# Revit family: 210_c64ea0e677dc4fbe8cce54dced4735
name_source: partatom
category: Mechanical Equipment
revit_build: Autodesk Revit 2018 (Build: 20170223_1515(x64)
units: mm (PartAtom-declared; Revit-internal decimal feet)

## family parameters
Always vertical = Yes
Cut with Voids When Loaded = No
Part Type = Breaks Into
Room Calculation Point = No
Round Connector Dimension = Use Diameter
Shared = No
Work Plane-Based = No

## types (1)
- K2 REL W (700016)
    Clearance Zone Front Depth = 638 mm  [stored 2.09318 ft]
    DEXH = 125 mm
    DEXT = 125 mm
    DL = 48 mm  [stored 0.15748 ft]
    DOUT = 125 mm
    DSUP = 125 mm
    Description = K2 REL W (700016)
    EXHX = 215 mm  [stored 0.705381 ft]
    EXHY = 129 mm  [stored 0.423228 ft]
    EXTX = 72 mm  [stored 0.23622 ft]
    EXTY = 229 mm  [stored 0.751312 ft]
    H2 = 385 mm  [stored 1.26312 ft]
    L1 = 30 mm  [stored 0.0984252 ft]
    L1__ve = -30 mm
    L2 = 299 mm  [stored 0.980971 ft]
    LM = 538 mm
    MC Product Code = K2 REL W (700016)
    Manufacturer = Flexit
    OUTX = 215 mm  [stored 0.705381 ft]
    OUTY = 229 mm  [stored 0.751312 ft]
    QmdConnectorList = 221;DSUP;231;DOUT;241;DEXT;251;DEXH
    REXH = 63 mm
    REXT = 63 mm
    ROUT = 63 mm
    RSUP = 63 mm
    SUPX = 72 mm  [stored 0.23622 ft]
    SUPY = 129 mm  [stored 0.423228 ft]
    W = 510 mm  [stored 1.67323 ft]
    W1 = 384 mm  [stored 1.25984 ft]
    magiPartTypeId = 210
    magiProductFamilyId = c64ea0e677dc4fbe8cce54dced4735
    magiProductId = c64ea0e677dc4fbe8cce54dced4735

note: [stored X ft] marks values corroborated as IEEE doubles in the binary element streams (Revit-internal decimal feet)

## geometry (parser evidence)
native form markers: Sweep x1
no freeform markers — native parametric forms only
